# Revit family: Gira_200900
name_source: partatom
category: Allgemeines Modell
revit_build: Autodesk Revit 2017 (Build: 20160225_1515(x64)
units: mm (PartAtom-declared; Revit-internal decimal feet)

## family parameters
Basisbauteil = Fläche
Beim Laden mit Abzugskörper schneiden = Nein
Bemaßung runder Anschluss = Durchmesser verwenden
Gemeinsam genutzt = Nein
Kann Basisbauteil für Bewehrung sein = Nein
Raumberechnungspunkt = Nein
Teiletyp = Normal

## types (1)
- Gira_200900
    BIM = https://media.stage.bim.site ext.Fühler KNX.rfa
    Beschreibung = Ins.bus coup.3 ext.sens. KNX,Insert for KNX bus coupler 3 with external sensor,,,Features:,- The bus coupler 3 connects the KNX system to a KNX application module.,- The combination of bus coupler 3 and application module represents a functional unit.,- In the ETS project, this unit is configured in the form of the application program of the application module.,- In addition, a remote temperature sensor can be connected to the bus coupler 3 with remote sensor. This enables a room temperature controller to record the temperature at an additional measuring point.,,Notes :,- The remote sensor functions only in combination with the pushbutton sensor 3 Plus.
    Bus system KNX = Ja
    Bus system KNX radio = Nein
    Bus system LON = Nein
    Bus system Powernet = Nein
    Bus system radio frequent = Nein
    Data sheet = https://katalog.gira.de
    GTIN = 4010337082194
    HAN = 200900
    Hersteller = Gira
    Mounting method = Flush mounted (plaster)
    Other bus systems = None
    Productwebsite = http://katalog.gira.de
    Type of fastening = Mounting with claw and screw
    Typname = Bus coup.3 external sens. KNX insert
    URL = https://www.gira.de
    Vorgabe-Ansicht = 1219 mm

## geometry (parser evidence)
native form markers: Sweep x2
no freeform markers — native parametric forms only
